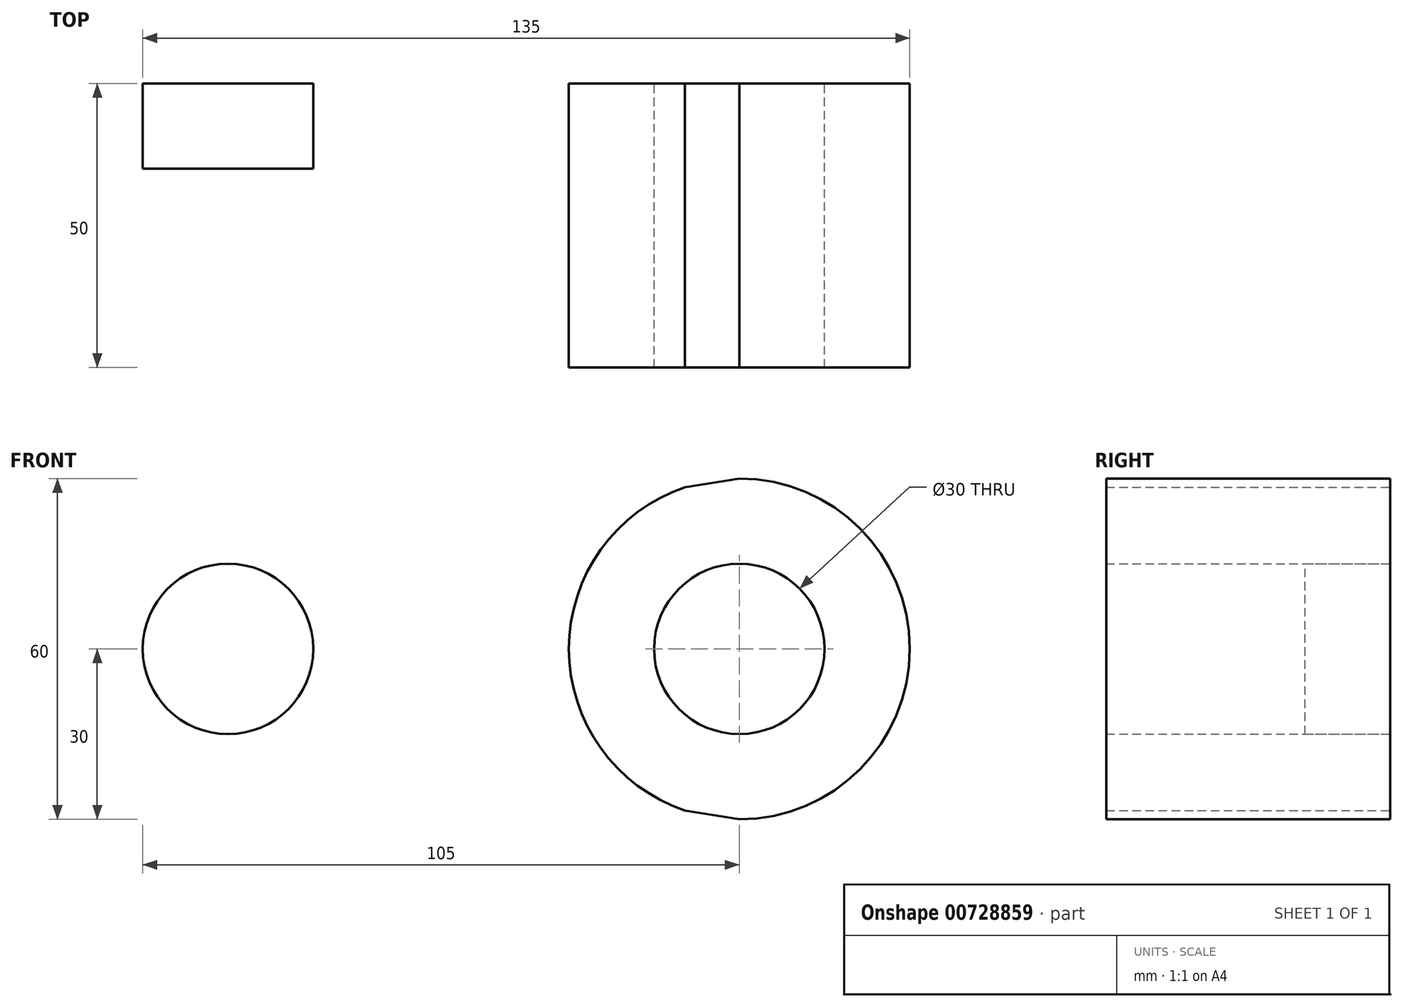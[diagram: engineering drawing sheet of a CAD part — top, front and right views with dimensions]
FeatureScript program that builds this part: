
annotation { "Feature Type Name" : "Feature", "Feature Type Description" : "" }
export const myFeature = defineFeature(function(context is Context, id is Id, definition is map)
    precondition{}
    {
        {
            var Q0;
            Q0=qCreatedBy(makeId("Front.planeOp"),FACE);
            var sketch = newSketch(context, id + "F0", { "sketchPlane" : qUnion([Q0])});
            skCircle(sketch, "E0", {"center": v(0, 0) * mm, "radius": 30 * mm});
            skCircle(sketch, "E1", {"center": v(0, 0) * mm, "radius": 15 * mm});
            skCircle(sketch, "E2", {"center": v(-90, 0) * mm, "radius": 15 * mm});
            skLineSegment(sketch, "E3", {"start": v(0, 30) * mm, "end": v(-92.43, 14.8) * mm});
            skLineSegment(sketch, "E4", {"start": v(0, -30) * mm, "end": v(-92.43, -14.8) * mm});
            skSolve(sketch);
        }
        {
            var Q0;
            Q0=makeQuery(id+"F0.imprint","IMPRINT",FACE,{"disambiguationData":[TD([[makeQuery(id+"F0.imprint","IMPRINT",EDGE,{"derivedFrom":sQuery(id+"F0.wireOp",EDGE,"E1")}),-1.0]])]});
            extrude(context, id + "F1", {"entities" : qUnion([Q0]), "depth" : 50 * mm, "offsetDistance" : 25 * mm});
        }
        {
            var Q0;
            {var subQ0=sQuery(id+"F0.wireOp",EDGE,"E3");var subQ1=sQuery(id+"F0.wireOp",EDGE,"E0");var subQ2=makeQuery(id+"F0.imprint","INTERSECT",VERTEX,{"disambiguationData":[OD(1.0)],"derivedFrom":[subQ1,subQ0]});Q0=makeQuery(id+"F0.imprint","IMPRINT",FACE,{"disambiguationData":[TD([[makeQuery(id+"F0.imprint","IMPRINT",EDGE,{"disambiguationData":[TD([[subQ2,-1.0]])],"derivedFrom":subQ1}),-1.0]])]});}
            var Q1;
            {var subQ0=sQuery(id+"F0.wireOp",EDGE,"E2");var subQ1=makeQuery(id+"F0.imprint","INTERSECT",VERTEX,{"derivedFrom":[subQ0,sQuery(id+"F0.wireOp",EDGE,"E3")]});Q1=makeQuery(id+"F0.imprint","IMPRINT",FACE,{"disambiguationData":[TD([[makeQuery(id+"F0.imprint","IMPRINT",EDGE,{"disambiguationData":[TD([[subQ1,-1.0]])],"derivedFrom":subQ0}),1.0]])]});}
            extrude(context, id + "F2", {"entities" : qUnion([Q0, Q1]), "operationType" : NewBodyOperationType.ADD, "depth" : 15 * mm, "offsetDistance" : 25 * mm});
        }
    });
